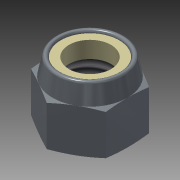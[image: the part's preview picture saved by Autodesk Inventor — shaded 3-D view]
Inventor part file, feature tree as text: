
AUTODESK INVENTOR PART (.ipt)
format: ipt  version: 2018 (Build 220112000, 112)  size: 205,312 bytes
history: native  units: mm (DEFAULTED — no unit token found)
features: sketch x5, extrude x2, revolve x2, other x1, plane x1, thread x1
ambient origin geometry x8: Origin, YZ Plane, XZ Plane, XY Plane, X Axis, Y Axis, Z Axis, Center Point
bodies: Solid1 (feature_tree)
feature tree (12):
  other  "Hexagon_flats_join1"
  extrude  "Extrusion1"  Depth=25.4mm TaperAngle=0.0deg
  revolve  "Revolution1"  Angle=90.0deg
  plane  "Work Plane1"
  extrude  "Extrusion2"  Depth=1.5875mm
  revolve  "Revolution2"  Angle=15.0deg
  thread  "Thread1"  [1 undecoded]
  sketch  "Sketch1"  dims[d0=14.2875mm d3=25.4mm d4=0.0mm]
  sketch  "Sketch2"  dims[d5=13.788101mm d7=90.0deg]
  sketch  "Sketch3"  dims[d9=25.4mm d10=0.0mm d11=1.5875mm]
  sketch  "Sketch4"  dims[d12=15.0deg d13=15.0deg d14=14.2875mm]
  sketch  "Sketch5"  dims[d15=90.0deg d16=25.4mm d17=0.0mm]
note: 1 required parameter value undecoded (feature->parameter linkage not recoverable at this tier; creation-order binding heuristic only, values carry confidence <= 0.55)
